# Revit family: Bourgeat - Armoires de décontamination
name_source: partatom
category: Equipement spécialisé
revit_build: Autodesk Revit 2015 (Build: 20140606_1530(x64)
units: mm (PartAtom-declared; Revit-internal decimal feet)

## types (8) — shared parameters
Fabricant = BOURGEAT
Fréquence = 50 Hz
Hauteur hors tout = 738 mm
Indice de protection = 21
Intensité nominale = 0 A
Phase = 2
Profondeur hors tout = 136 mm
Spécification du Fabricant = Armoires de décontamination
Tension = 230 V
URL catalogue = http://www.bourgeat.fr

## per-type parameters (varying)
| type | Avec Serrure | Barre Aimantée | Double porte | Longueur hors tout | Modèle | Nombre de fil | Panier fil inox | Poids net à vide | Poids à vide | Puissance électrique  |
| Pour 10 couteaux barre aimantée sans serrure | Non | Oui | Non | 587 mm  [stored 1.92585 ft] | 855605 | 2 | Non | 9.50 kg | 9.5 kg | 18 W |
| Pour 40 couteaux barre aimantée sans serrure | Non | Oui | Oui | 1080 mm  [stored 3.54331 ft] | 855630 | 2 | Non | 15.00 kg | 15 kg | 34 W |
| Pour 10 couteaux barre aimantée avec serrure | Oui | Oui | Non | 587 mm  [stored 1.92585 ft] | 855606 | 2 | Non | 9.50 kg | 9.5 kg | 18 W |
| Pour 40 couteaux barre aimantée avec serrure | Oui | Oui | Oui | 1080 mm  [stored 3.54331 ft] | 855631 | 2 | Non | 15.00 kg | 15 kg | 34 W |
| Pour 20 couteaux panier fil inox avec serrure | Oui | Non | Non | 587 mm  [stored 1.92585 ft] | 855616 | 40 | Oui | 9.50 kg | 9.5 kg | 18 W |
| Pour 20 couteaux panier fil inox sans serrure | Non | Non | Non | 587 mm  [stored 1.92585 ft] | 855615 | 40 | Oui | 9.50 kg | 9.5 kg | 18 W |
| Pour 40 couteaux panier fil inox sans serrure | Non | Non | Oui | 1080 mm  [stored 3.54331 ft] | 855640 | 80 | Oui | 15.00 kg | 15 kg | 34 W |
| Pour 40 couteaux panier fil inox avec serrure | Oui | Non | Oui | 1080 mm  [stored 3.54331 ft] | 855641 | 80 | Oui | 15.00 kg | 15 kg | 34 W |

note: [stored X ft] marks values corroborated as IEEE doubles in the binary element streams (Revit-internal decimal feet)
